# Revit family: Gira_228403
name_source: partatom
category: Elektroinstallationen
revit_build: Autodesk Revit 2017 (Build: 20160225_1515(x64)
units: mm (PartAtom-declared; Revit-internal decimal feet)

## family parameters
Basisbauteil = Fläche
Beim Laden mit Abzugskörper schneiden = Nein
Bemaßung runder Anschluss = Durchmesser verwenden
Beschriftungsausrichtung beibehalten = Ja
Gemeinsam genutzt = Nein
Raumberechnungspunkt = Nein
Teiletyp = Normal

## types (1)
- UP-Radio RDS o.Lautsprecher System 55 Reinweiß
    Anschlussart = Steckklemme
    Anzahl der Betätigungswippen = 2
    Anzahl der Module (bei Modulbauweise) = 1
    Ausführung = Radio (*en-EN)
    Ausführung der Oberfläche = glänzend
    Bedienungsart = Wippe/Taste
    Befestigungsart = Krallen-/Schraubbefestigung
    Beleuchtung = nein
    Bemessungsstrom = 10 Ampere
    Beschreibung = Unterputz-Radio RDS  Reinweiß glänzend
    Farbe = aluminium
    GTIN = 4010337889212
    Geeignet für Schutzart (IP) = IP20
    HAN = 1104005
    Halogenfrei = Ja
    HeinzeBIM = https://bimportal.heinze.de
    Hersteller = Gira
    Kategorie = Installationsschalter
    Mit Montageplatte = Nein
    Modell = Sys55_Komplettgerät_Schalten und Tasten
    Montageart = unter Putz
    Name = Wippschalter Anzeige Hotelzimmerstatus System 55 Schwarz m
    Nennspannung = 250 Volt
    Oberfläche = sonstige
    RAL-Nummer (ähnlich) = 9010
    Region = DE
    Rückmeldekontakt = Nein
    Schaltungsart = Serienschalter
    Tastschalter = Nein
    Textfeld/Beschriftungsfläche = nein
    URL = http://katalog.gira.de
    Verfügbar = Ja
    Vorgabe-Ansicht = 1219 mm
    Waschmaschinenschalter = Nein
    Werkstoff = sonstige
    Werkstoffgüte = sonstige
    Zusammenstellung = Basiselement mit zentraler Abdeckplatte

## geometry (parser evidence)
native form markers: Sweep x8
no freeform markers — native parametric forms only
